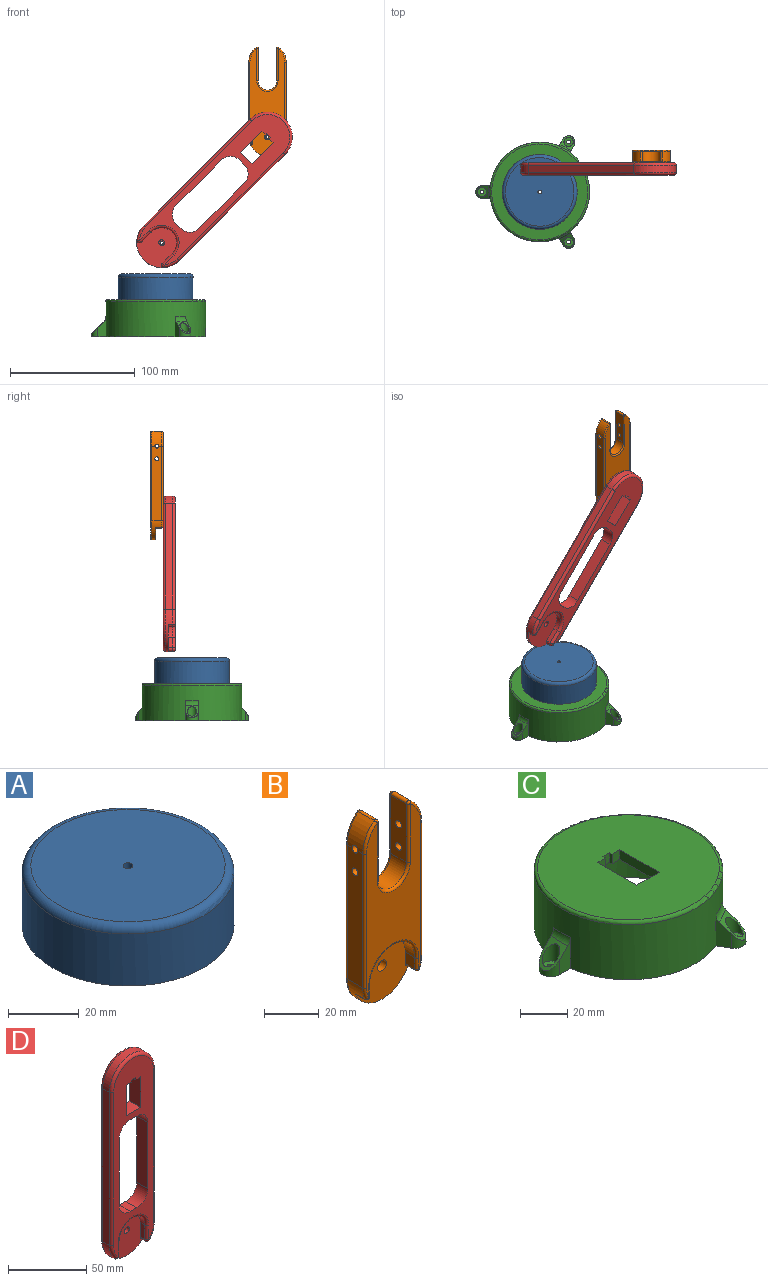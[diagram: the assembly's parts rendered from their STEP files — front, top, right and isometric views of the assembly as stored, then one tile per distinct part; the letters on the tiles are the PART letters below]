
ASSEMBLY  parts=4 mates=2
PART A: 31 faces, bbox 64.9x64.9x20.5 mm
  f0: plane 29.83x13.43mm, normal (0,0,-1), area 267.2mm2, adj f2,f12,f19,f20,f21,f22,f23,f24
  f1: cylinder r=2.5mm len=5mm, axis (0,0,-1), area 41.6mm2, adj f10,f14
  f2: cylinder r=15mm len=30mm, axis (0,0,-1), area 694.2mm2, adj f0,f4,f5,f12,f13,f14,f18,f26
  f3: cylinder r=25mm len=50mm, axis (0,0,-1), area 2827.4mm2, adj f4,f6
  f4: plane 50x50mm, normal (0,0,-1), area 1256.6mm2, adj f2,f3
  f5: plane 29.83x13.43mm, normal (0,0,-1), area 267.2mm2, adj f2,f13,f15,f16,f17,f18,f27,f28
  f6: plane 60x60mm, normal (0,0,-1), area 863.9mm2, adj f3,f9
  f7: plane 55x55mm, normal (0,0,1), area 2369.7mm2, adj f8,f11
  f8: torus R=27.5mm, axis (0,0,1), area 717.8mm2, adj f7,f9
  f9: cylinder r=30mm len=60mm, axis (0,0,-1), area 3392.9mm2, adj f6,f8
  f10: plane 5x5mm, normal (0,0,-1), area 13.5mm2, adj f1,f11
  f11: cylinder r=1.4mm len=5.35mm, axis (0,0,-1), area 47.1mm2, adj f7,f10
  f12: cylinder r=1.78mm len=2mm, axis (0,0,-1), area 1.4mm2, adj f0,f2,f14,f19
  f13: cylinder r=1.78mm len=2mm, axis (0,0,-1), area 1.4mm2, adj f2,f5,f14,f27
  f14: plane 30x14.79mm, normal (0,0,-1), area 152.8mm2, adj f1,f2,f12,f13,f15,f16,f17,f18
  f15: plane 2.48x2mm, normal (-1,0,0), area 5mm2, adj f5,f14,f16,f30
  f16: cylinder r=3.54mm len=2mm, axis (0,0,-1), area 0.5mm2, adj f5,f14,f15,f17
  f17: plane 12.04x2mm, normal (-0.08,-1,0), area 24.2mm2, adj f5,f14,f16,f18
  f18: cylinder r=1.78mm len=2mm, axis (0,0,-1), area 1.4mm2, adj f2,f5,f14,f17
  f19: plane 12.04x2mm, normal (-0.08,1,0), area 24.2mm2, adj f0,f12,f14,f20
  f20: cylinder r=3.54mm len=2mm, axis (0,0,-1), area 0.5mm2, adj f0,f14,f19,f21
  f21: plane 2.48x2mm, normal (-1,0,0), area 5mm2, adj f0,f14,f20,f22
  f22: cylinder r=2mm len=4mm, axis (0,0,-1), area 12.6mm2, adj f0,f14,f21,f23
  f23: plane 2.48x2mm, normal (1,0,0), area 5mm2, adj f0,f14,f22,f24
  f24: cylinder r=3.54mm len=2mm, axis (0,0,-1), area 0.5mm2, adj f0,f14,f23,f25
  f25: plane 12.04x2mm, normal (0.08,1,0), area 24.2mm2, adj f0,f14,f24,f26
  f26: cylinder r=1.78mm len=2mm, axis (0,0,-1), area 1.4mm2, adj f0,f2,f14,f25
  f27: plane 12.04x2mm, normal (0.08,-1,0), area 24.2mm2, adj f5,f13,f14,f28
  f28: cylinder r=3.54mm len=2mm, axis (0,0,-1), area 0.5mm2, adj f5,f14,f27,f29
  f29: plane 2.48x2mm, normal (1,0,0), area 5mm2, adj f5,f14,f28,f30
  f30: cylinder r=2mm len=4mm, axis (0,0,-1), area 12.6mm2, adj f5,f14,f15,f29
PART B: 51 faces, bbox 32.5x10x89.1 mm
  f0: cylinder r=15mm len=11.92mm, axis (0,1,0), area 106.6mm2, adj f2,f4,f29,f34,f41
  f1: plane 85.12x28mm, normal (0,1,0), area 1699.9mm2, adj f14,f38,f41,f42,f44,f45,f47,f49
  f2: cylinder r=1.51mm len=7.5mm, axis (-1,0,0), area 71.1mm2, adj f0,f4,f16
  f3: plane 60x8mm, normal (-1,0,0), area 469.3mm2, adj f5,f6,f15,f19,f36,f49
  f4: plane 60x8mm, normal (1,0,0), area 469.3mm2, adj f0,f2,f6,f20,f26,f44
  f5: cylinder r=15mm len=11.92mm, axis (0,1,0), area 106.6mm2, adj f3,f15,f40,f46,f50
  f6: cylinder r=15mm len=30mm, axis (0,1,0), area 198.4mm2, adj f3,f4,f11,f21,f24,f28,f33,f47
  f7: plane 76.32x28mm, normal (0,-1,0), area 1138.5mm2, adj f23,f24,f25,f26,f27,f29,f32,f33
  f8: cylinder r=12mm len=24mm, axis (0,-1,0), area 188.5mm2, adj f9,f10,f11,f25
  f9: plane 5.2x5mm, normal (1,0,0), area 26mm2, adj f8,f11,f27,f28
  f10: plane 5.2x5mm, normal (-1,0,0), area 26mm2, adj f8,f11,f21,f23
  f11: plane 27.86x27mm, normal (0,-1,0), area 531.8mm2, adj f6,f8,f9,f10,f12,f21,f28
  f12: cylinder r=2.3mm len=4.6mm, axis (0,-1,0), area 43.4mm2, adj f11,f13
  f13: plane 4.6x4.6mm, normal (0,-1,0), area 11.7mm2, adj f12,f14
  f14: cylinder r=1.25mm len=2.5mm, axis (0,-1,0), area 7.9mm2, adj f1,f13
  f15: cylinder r=1.51mm len=7.5mm, axis (-1,0,0), area 71.1mm2, adj f3,f5,f17
  f16: plane 26.12x8mm, normal (-1,0,0), area 194.7mm2, adj f2,f18,f20,f32,f34,f38
  f17: plane 26.12x8mm, normal (1,0,0), area 194.7mm2, adj f15,f18,f19,f39,f45,f46
  f18: cylinder r=7.5mm len=15mm, axis (0,1,0), area 188.5mm2, adj f16,f17,f35,f42
  f19: cylinder r=1.5mm len=7.5mm, axis (1,0,0), area 70.7mm2, adj f3,f17
  f20: cylinder r=1.5mm len=7.5mm, axis (1,0,0), area 70.7mm2, adj f4,f16
  f21: cylinder r=1mm len=5mm, axis (0,1,0), area 13.8mm2, adj f6,f10,f11,f22
  f22: sphere r=1mm, area 2.8mm2, adj f21,f23,f24
  f23: cylinder r=1mm len=5.2mm, axis (0,0,-1), area 8.2mm2, adj f7,f10,f22,f25
  f24: torus R=14mm, axis (0,-1,0), area 8.7mm2, adj f6,f7,f22,f26
  f25: torus R=13mm, axis (0,-1,0), area 61mm2, adj f7,f8,f23,f27
  f26: cylinder r=1mm len=60mm, axis (0,0,-1), area 94.2mm2, adj f4,f7,f24,f29
  f27: cylinder r=1mm len=5.2mm, axis (0,0,1), area 8.2mm2, adj f7,f9,f25,f30
  f28: cylinder r=1mm len=5mm, axis (0,1,0), area 13.8mm2, adj f6,f9,f11,f30
  f29: torus R=14mm, axis (0,-1,0), area 21.1mm2, adj f0,f7,f26,f31
  f30: sphere r=1mm, area 2.8mm2, adj f27,f28,f33
  f31: sphere r=1mm, area 2.2mm2, adj f29,f32,f34
  f32: cylinder r=1mm len=26.12mm, axis (0,0,-1), area 41mm2, adj f7,f16,f31,f35
  f33: torus R=14mm, axis (0,-1,0), area 8.7mm2, adj f6,f7,f30,f36
  f34: cylinder r=1mm len=8mm, axis (0,1,0), area 17.8mm2, adj f0,f16,f31,f37
  f35: torus R=8.5mm, axis (0,-1,0), area 38.8mm2, adj f7,f18,f32,f39
  f36: cylinder r=1mm len=60mm, axis (0,0,1), area 94.2mm2, adj f3,f7,f33,f40
  f37: sphere r=1mm, area 2.2mm2, adj f34,f38,f41
  f38: cylinder r=1mm len=26.12mm, axis (0,0,-1), area 41mm2, adj f1,f16,f37,f42
  f39: cylinder r=1mm len=26.12mm, axis (0,0,1), area 41mm2, adj f7,f17,f35,f43
  f40: torus R=14mm, axis (0,-1,0), area 21.1mm2, adj f5,f7,f36,f43
  f41: torus R=14mm, axis (0,-1,0), area 21.1mm2, adj f0,f1,f37,f44
  f42: torus R=8.5mm, axis (0,-1,0), area 38.8mm2, adj f1,f18,f38,f45
  f43: sphere r=1mm, area 2.2mm2, adj f39,f40,f46
  f44: cylinder r=1mm len=60mm, axis (0,0,1), area 94.2mm2, adj f1,f4,f41,f47
  f45: cylinder r=1mm len=26.12mm, axis (0,0,1), area 41mm2, adj f1,f17,f42,f48
  f46: cylinder r=1mm len=8mm, axis (0,1,0), area 17.8mm2, adj f5,f17,f43,f48
  f47: torus R=14mm, axis (0,-1,0), area 72.2mm2, adj f1,f6,f44,f49
  f48: sphere r=1mm, area 2.2mm2, adj f45,f46,f50
  f49: cylinder r=1mm len=60mm, axis (0,0,-1), area 94.2mm2, adj f1,f3,f47,f50
  f50: torus R=14mm, axis (0,-1,0), area 21.1mm2, adj f1,f5,f48,f49
PART C: 41 faces, bbox 94.8x94.6x30.1 mm
  f0: plane 5x4.63mm, normal (0,-1,0), area 23.1mm2, adj f2,f3,f8,f39
  f1: cylinder r=40mm len=80mm, axis (0,0,-1), area 6644.6mm2, adj f4,f5,f11,f12,f13,f14,f16,f17
  f2: plane 77x77mm, normal (0,0,1), area 4339.3mm2, adj f0,f5,f7,f8,f9,f10,f38,f39
  f3: plane 70x70mm, normal (0,0,-1), area 3531.1mm2, adj f0,f6,f7,f8,f9,f10,f38,f39
  f4: plane 91.29x90.32mm, normal (0,0,-1), area 1444mm2, adj f1,f6,f11,f13,f14,f15,f16,f17
  f5: torus R=38.5mm, axis (0,0,1), area 584.1mm2, adj f1,f2
  f6: cylinder r=35mm len=70mm, axis (0,0,-1), area 5462.9mm2, adj f3,f4,f11,f12,f13
  f7: plane 5x4.63mm, normal (0,-1,0), area 23.1mm2, adj f2,f3,f10,f40
  f8: plane 23.5x5mm, normal (1,0,0), area 117.5mm2, adj f0,f2,f3,f9
  f9: plane 13.25x5mm, normal (0,1,0), area 66.3mm2, adj f2,f3,f8,f10
  f10: plane 23.5x5mm, normal (-1,0,0), area 117.5mm2, adj f2,f3,f7,f9
  f11: plane 5.01x5mm, normal (0,-1,0), area 25.1mm2, adj f1,f4,f6,f12
  f12: cylinder r=2.5mm len=5.09mm, axis (-1,0,0), area 39.3mm2, adj f1,f6,f11,f13
  f13: plane 5.01x5mm, normal (0,1,0), area 25.1mm2, adj f1,f4,f6,f12
  f14: plane 16.15x6.77mm, normal (0,-1,0), area 71.9mm2, adj f1,f4,f15,f25,f37
  f15: cylinder r=5mm len=10mm, axis (0,0,-1), area 67.8mm2, adj f4,f14,f16,f25
  f16: plane 16.15x6.77mm, normal (0,1,0), area 71.9mm2, adj f1,f4,f15,f25,f37
  f17: plane 16.15x5.87mm, normal (0.87,-0.5,0), area 71.9mm2, adj f1,f4,f19,f23,f35
  f18: plane 16.15x5.87mm, normal (-0.87,0.5,0), area 71.9mm2, adj f1,f4,f19,f23,f35
  f19: cylinder r=5mm len=9.33mm, axis (0,0,-1), area 67.8mm2, adj f4,f17,f18,f23
  f20: plane 16.15x5.87mm, normal (-0.87,-0.5,0), area 71.9mm2, adj f1,f4,f22,f24,f36
  f21: plane 16.15x5.87mm, normal (0.87,0.5,0), area 71.9mm2, adj f1,f4,f22,f24,f36
  f22: cylinder r=5mm len=9.33mm, axis (0,0,-1), area 67.8mm2, adj f4,f20,f21,f24
  f23: cone r=40mm half-angle=45deg, axis (0,0,-1), area 64.1mm2, adj f17,f18,f19,f29,f35
  f24: cone r=40mm half-angle=45deg, axis (0,0,-1), area 64mm2, adj f20,f21,f22,f31,f36
  f25: cone r=40mm half-angle=45deg, axis (0,0,-1), area 64mm2, adj f14,f15,f16,f33,f37
  f26: cylinder r=1.5mm len=3mm, axis (0,0,-1), area 18.8mm2, adj f4,f34
  f27: cylinder r=1.5mm len=3mm, axis (0,0,-1), area 18.8mm2, adj f4,f32
  f28: cylinder r=1.5mm len=3mm, axis (0,0,-1), area 18.8mm2, adj f4,f30
  f29: cylinder r=3.75mm len=9.38mm, axis (0,0,-1), area 130.9mm2, adj f23,f30
  f30: plane 7.5x7.5mm, normal (0,0,1), area 37.1mm2, adj f28,f29
  f31: cylinder r=3.75mm len=9.38mm, axis (0,0,-1), area 130.8mm2, adj f24,f32
  f32: plane 7.5x7.5mm, normal (0,0,1), area 37.1mm2, adj f27,f31
  f33: cylinder r=3.75mm len=9.38mm, axis (0,0,-1), area 130.8mm2, adj f25,f34
  f34: plane 7.5x7.5mm, normal (0,0,1), area 37.1mm2, adj f26,f33
  f35: torus R=45mm, axis (0,0,1), area 39.2mm2, adj f1,f17,f18,f23
  f36: torus R=45mm, axis (0,0,1), area 39.2mm2, adj f1,f20,f21,f24
  f37: torus R=45mm, axis (0,0,1), area 39.2mm2, adj f1,f14,f16,f25
  f38: plane 5x4mm, normal (0,-1,0), area 20mm2, adj f2,f3,f39,f40
  f39: plane 5x1.5mm, normal (1,0,0), area 7.5mm2, adj f0,f2,f3,f38
  f40: plane 5x1.5mm, normal (-1,0,0), area 7.5mm2, adj f2,f3,f7,f38
PART D: 45 faces, bbox 43.3x10x163.3 mm
  f0: plane 10x4.5mm, normal (0,0,-1), area 45mm2, adj f2,f3,f9,f36
  f1: cylinder r=1.25mm len=2.5mm, axis (0,-1,0), area 3.9mm2, adj f3,f16
  f2: plane 149.31x36mm, normal (0,-1,0), area 2478.7mm2, adj f0,f8,f9,f10,f11,f20,f21,f22
  f3: plane 156x36mm, normal (0,1,0), area 3228.8mm2, adj f0,f1,f8,f9,f10,f11,f30,f31
  f4: plane 120x6mm, normal (1,0,0), area 720mm2, adj f5,f7,f28,f33
  f5: cylinder r=20mm len=40mm, axis (0,1,0), area 377mm2, adj f4,f6,f26,f31
  f6: plane 120x6mm, normal (-1,0,0), area 720mm2, adj f5,f7,f23,f30
  f7: cylinder r=20mm len=40mm, axis (0,1,0), area 234.4mm2, adj f4,f6,f12,f18,f21,f24,f29,f32
  f8: plane 13x10mm, normal (0,0,1), area 130mm2, adj f2,f3,f9,f11
  f9: plane 24x10mm, normal (-1,0,0), area 240mm2, adj f0,f2,f3,f8
  f10: plane 10x4.5mm, normal (0,0,-1), area 45mm2, adj f2,f3,f11,f35
  f11: plane 24x10mm, normal (1,0,0), area 240mm2, adj f2,f3,f8,f10
  f12: plane 32x31.11mm, normal (0,-1,0), area 669.4mm2, adj f7,f13,f14,f15,f17,f18,f24
  f13: cylinder r=12mm len=24mm, axis (0,-1,0), area 150.8mm2, adj f12,f14,f15,f22
  f14: plane 11.31x4mm, normal (1,0,0), area 45.3mm2, adj f12,f13,f18,f20
  f15: plane 11.31x4mm, normal (-1,0,0), area 45.3mm2, adj f12,f13,f24,f25
  f16: plane 4.59x4.59mm, normal (0,-1,0), area 11.6mm2, adj f1,f17
  f17: cylinder r=2.29mm len=4.59mm, axis (0,-1,0), area 50.4mm2, adj f12,f16
  f18: cylinder r=2mm len=4mm, axis (0,1,0), area 19.7mm2, adj f7,f12,f14,f19
  f19: sphere r=2mm, area 9.8mm2, adj f18,f20,f21
  f20: cylinder r=2mm len=11.31mm, axis (0,0,1), area 35.5mm2, adj f2,f14,f19,f22
  f21: torus R=18mm, axis (0,-1,0), area 41.2mm2, adj f2,f7,f19,f23
  f22: torus R=14mm, axis (0,-1,0), area 125.6mm2, adj f2,f13,f20,f25
  f23: cylinder r=2mm len=120mm, axis (0,0,1), area 377mm2, adj f2,f6,f21,f26
  f24: cylinder r=2mm len=4mm, axis (0,1,0), area 19.7mm2, adj f7,f12,f15,f27
  f25: cylinder r=2mm len=11.31mm, axis (0,0,-1), area 35.5mm2, adj f2,f15,f22,f27
  f26: torus R=18mm, axis (0,-1,0), area 190.2mm2, adj f2,f5,f23,f28
  f27: sphere r=2mm, area 9.8mm2, adj f24,f25,f29
  f28: cylinder r=2mm len=120mm, axis (0,0,-1), area 377mm2, adj f2,f4,f26,f29
  f29: torus R=18mm, axis (0,-1,0), area 41.2mm2, adj f2,f7,f27,f28
  f30: cylinder r=2mm len=120mm, axis (0,0,-1), area 377mm2, adj f3,f6,f31,f32
  f31: torus R=18mm, axis (0,-1,0), area 190.2mm2, adj f3,f5,f30,f33
  f32: torus R=18mm, axis (0,-1,0), area 190.2mm2, adj f3,f7,f30,f33
  f33: cylinder r=2mm len=120mm, axis (0,0,1), area 377mm2, adj f3,f4,f31,f32
  f34: plane 10x4mm, normal (0,0,-1), area 40mm2, adj f2,f3,f35,f36
  f35: plane 10x1.5mm, normal (1,0,0), area 15mm2, adj f2,f3,f10,f34
  f36: plane 10x1.5mm, normal (-1,0,0), area 15mm2, adj f0,f2,f3,f34
  f37: plane 52x10mm, normal (-1,0,0), area 520mm2, adj f2,f3,f38,f44
  f38: cylinder r=10mm len=10mm, axis (0,-1,0), area 157.1mm2, adj f2,f3,f37,f39
  f39: plane 10x6mm, normal (0,0,-1), area 60mm2, adj f2,f3,f38,f40
  f40: cylinder r=10mm len=10mm, axis (0,-1,0), area 157.1mm2, adj f2,f3,f39,f41
  f41: plane 52x10mm, normal (1,0,0), area 520mm2, adj f2,f3,f40,f42
  f42: cylinder r=10mm len=10mm, axis (0,-1,0), area 157.1mm2, adj f2,f3,f41,f43
  f43: plane 10x6mm, normal (0,0,1), area 60mm2, adj f2,f3,f42,f44
  f44: cylinder r=10mm len=10mm, axis (0,-1,0), area 157.1mm2, adj f2,f3,f37,f43
PLACE A t=(-87.67,-42.76,8.17)mm
PLACE B t=(1.96,-9.5,160.75)mm
PLACE C t=(-87.67,-42.75,-32.33)mm
PLACE D rot(axis=(0,1,0),45deg) t=(-40.47,-19.5,85.68)mm
MATE revolute D.f5 <-> B.f6  axis (0,1,0) through (1.96,-19.5,128.11)mm
MATE revolute A.f3 <-> C.f2  axis (0,0,-1) through (-87.67,-42.76,-2.33)mm
